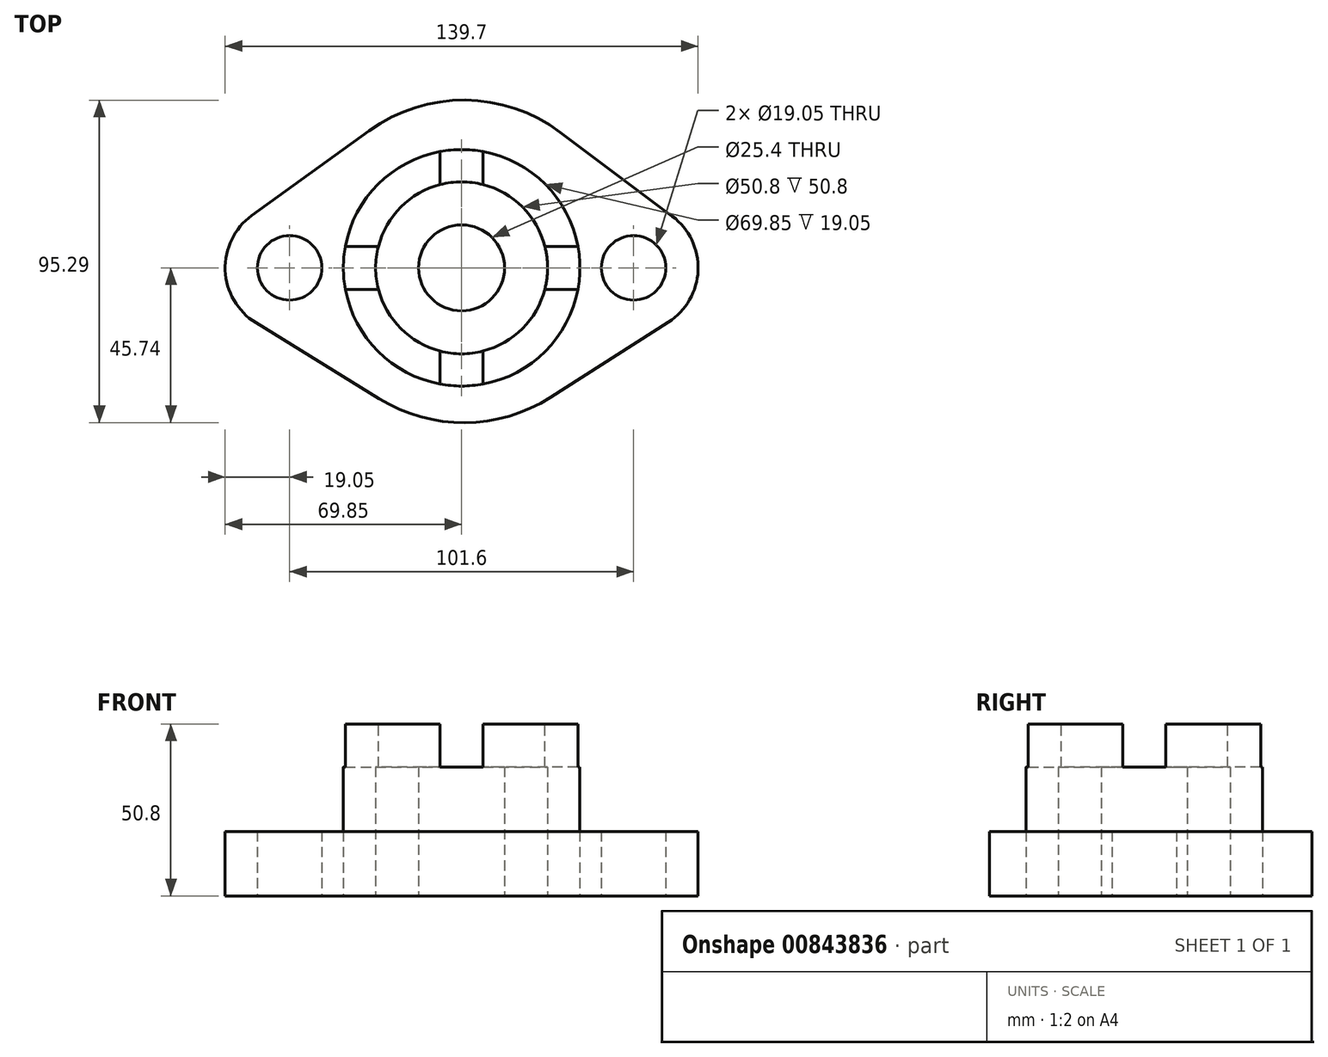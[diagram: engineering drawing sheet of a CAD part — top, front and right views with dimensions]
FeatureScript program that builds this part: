
annotation { "Feature Type Name" : "Feature", "Feature Type Description" : "" }
export const myFeature = defineFeature(function(context is Context, id is Id, definition is map)
    precondition{}
    {
        {
            var Q0;
            Q0=qCreatedBy(makeId("Top.planeOp"),FACE);
            var sketch = newSketch(context, id + "F0", { "sketchPlane" : qUnion([Q0])});
            skCircle(sketch, "E0", {"center": v(0, 0) * mm, "radius": 12.7 * mm});
            skCircle(sketch, "E1", {"center": v(0, 0) * mm, "radius": 34.93 * mm});
            skCircle(sketch, "E2", {"center": v(0, 0) * mm, "radius": 25.4 * mm});
            skLineSegment(sketch, "E3", {"start": v(0, 0) * mm, "end": v(88.9, 0) * mm, "construction": true});
            skLineSegment(sketch, "E4", {"start": v(88.9, 0) * mm, "end": v(-88.9, 0) * mm, "construction": true});
            skCircle(sketch, "E5", {"center": v(-50.8, 0) * mm, "radius": 9.53 * mm});
            skCircle(sketch, "E6", {"center": v(50.8, 0) * mm, "radius": 9.53 * mm});
            skArc(sketch, "E7", {"start": v(-61.97, 15.43) * mm, "mid": v(-69.84, -0.7) * mm, "end": v(-60.8, -16.22) * mm});
            skArc(sketch, "E8", {"start": v(61.05, -16.06) * mm, "mid": v(69.84, -0.72) * mm, "end": v(62.23, 15.24) * mm});
            skArc(sketch, "E9.trimOffspring", {"start": v(-24.37, -38.66) * mm, "mid": v(1, -45.74) * mm, "end": v(26.25, -38.26) * mm});
            skArc(sketch, "E10.trimOffspring", {"start": v(29.22, 40.01) * mm, "mid": v(1.04, 49.55) * mm, "end": v(-27.3, 40.5) * mm});
            skLineSegment(sketch, "E11", {"start": v(-61.97, 15.43) * mm, "end": v(-27.3, 40.5) * mm});
            skLineSegment(sketch, "E12", {"start": v(-60.8, -16.22) * mm, "end": v(-24.37, -38.66) * mm});
            skLineSegment(sketch, "E13", {"start": v(62.23, 15.24) * mm, "end": v(29.22, 40.01) * mm});
            skLineSegment(sketch, "E14", {"start": v(61.05, -16.06) * mm, "end": v(26.25, -38.26) * mm});
            skPoint(sketch, "E14.endSnap0", {"position": v(14.53, -43.66) * mm});
            skPoint(sketch, "E15.orphan", {"position": v(14.53, -45.74) * mm});
            skLineSegment(sketch, "E16", {"start": v(0, 0) * mm, "end": v(0, -51.53) * mm, "construction": true});
            skLineSegment(sketch, "E17", {"start": v(0, -51.53) * mm, "end": v(0, 57.86) * mm, "construction": true});
            skLineSegment(sketch, "E18", {"start": v(-30.1, 6.35) * mm, "end": v(-34.34, 6.35) * mm});
            skLineSegment(sketch, "E19", {"start": v(-30.1, 6.35) * mm, "end": v(-24.6, 6.35) * mm});
            skLineSegment(sketch, "E20", {"start": v(-30.1, -6.35) * mm, "end": v(-34.34, -6.35) * mm});
            skLineSegment(sketch, "E21", {"start": v(-30.1, -6.35) * mm, "end": v(-24.6, -6.35) * mm});
            skLineSegment(sketch, "E22", {"start": v(30.44, 6.35) * mm, "end": v(34.34, 6.35) * mm});
            skLineSegment(sketch, "E23", {"start": v(30.44, 6.35) * mm, "end": v(24.6, 6.35) * mm});
            skLineSegment(sketch, "E24", {"start": v(30.44, -6.35) * mm, "end": v(34.34, -6.35) * mm});
            skLineSegment(sketch, "E25", {"start": v(30.44, -6.35) * mm, "end": v(24.6, -6.35) * mm});
            skLineSegment(sketch, "E26", {"start": v(-6.35, 30.62) * mm, "end": v(-6.35, 34.34) * mm});
            skLineSegment(sketch, "E27", {"start": v(-6.35, 34.34) * mm, "end": v(-6.35, 24.6) * mm});
            skLineSegment(sketch, "E28", {"start": v(6.35, 30.62) * mm, "end": v(6.35, 34.34) * mm});
            skLineSegment(sketch, "E29", {"start": v(6.35, 34.34) * mm, "end": v(6.35, 24.6) * mm});
            skPoint(sketch, "E29.endSnap0", {"position": v(6.35, 32.48) * mm});
            skLineSegment(sketch, "E30", {"start": v(-6.35, -30.57) * mm, "end": v(-6.35, -24.6) * mm});
            skLineSegment(sketch, "E31", {"start": v(-6.35, -24.6) * mm, "end": v(-6.35, -34.34) * mm});
            skLineSegment(sketch, "E32", {"start": v(6.35, -30.57) * mm, "end": v(6.35, -24.6) * mm});
            skLineSegment(sketch, "E33", {"start": v(6.35, -24.6) * mm, "end": v(6.35, -34.34) * mm});
            skSolve(sketch);
        }
        {
            var Q0;
            Q0=makeQuery(id+"F0.imprint","IMPRINT",FACE,{"disambiguationData":[TD([[makeQuery(id+"F0.imprint","IMPRINT",EDGE,{"derivedFrom":sQuery(id+"F0.wireOp",EDGE,"E1")}),-1.0]])]});
            extrude(context, id + "F1", {"entities" : qUnion([Q0]), "depth" : 19.05 * mm, "offsetDistance" : 25.4 * mm});
        }
        {
            var Q0;
            Q0=makeQuery(id+"F0.imprint","IMPRINT",FACE,{"disambiguationData":[TD([[makeQuery(id+"F0.imprint","IMPRINT",EDGE,{"derivedFrom":sQuery(id+"F0.wireOp",EDGE,"E0")}),-1.0]])]});
            extrude(context, id + "F2", {"entities" : qUnion([Q0]), "depth" : 38.1 * mm, "offsetDistance" : 25.4 * mm});
        }
        {
            var Q0;
            Q0=makeQuery(id+"F0.imprint","IMPRINT",FACE,{"disambiguationData":[TD([[makeQuery(id+"F0.imprint","IMPRINT",EDGE,{"derivedFrom":sQuery(id+"F0.wireOp",EDGE,"E1")}),1.0]])]});
            extrude(context, id + "F3", {"entities" : qUnion([Q0]), "depth" : 50.8 * mm, "offsetDistance" : 25.4 * mm});
        }
        {
            var Q0;
            Q0=makeQuery(id+"F3.opExtrude","CAP_FACE",FACE,{"disambiguationData":[OSD([sQuery(id+"F0.wireOp",EDGE,"E1"),sQuery(id+"F0.wireOp",EDGE,"E2")])],"isStart":false});
            var sketch = newSketch(context, id + "F4", { "sketchPlane" : qUnion([Q0])});
            skLineSegment(sketch, "E34.left", {"start": v(6.35, 34.34) * mm, "end": v(6.35, 24.6) * mm});
            skLineSegment(sketch, "E34.right", {"start": v(-6.35, 34.34) * mm, "end": v(-6.35, 24.6) * mm});
            skPoint(sketch, "E34.middle", {"position": v(0, 25.4) * mm});
            skLineSegment(sketch, "E35.bottom", {"start": v(34.34, -6.35) * mm, "end": v(24.6, -6.35) * mm});
            skLineSegment(sketch, "E35.top", {"start": v(34.34, 6.35) * mm, "end": v(24.6, 6.35) * mm});
            skPoint(sketch, "E35.middle", {"position": v(25.4, 0) * mm});
            skLineSegment(sketch, "E36.left", {"start": v(6.35, -34.34) * mm, "end": v(6.35, -24.6) * mm});
            skLineSegment(sketch, "E36.right", {"start": v(-6.35, -34.34) * mm, "end": v(-6.35, -24.6) * mm});
            skPoint(sketch, "E36.middle", {"position": v(0, -25.4) * mm});
            skLineSegment(sketch, "E37.bottom", {"start": v(-34.34, 6.35) * mm, "end": v(-24.6, 6.35) * mm});
            skLineSegment(sketch, "E37.top", {"start": v(-34.34, -6.35) * mm, "end": v(-24.6, -6.35) * mm});
            skPoint(sketch, "E37.middle", {"position": v(-25.4, 0) * mm});
            skPoint(sketch, "E38", {"position": v(-24.6, 6.35) * mm});
            skPoint(sketch, "E39", {"position": v(-24.6, -6.35) * mm});
            skPoint(sketch, "E40", {"position": v(6.35, -24.6) * mm});
            skPoint(sketch, "E40.positionSnap0", {"position": v(6.35, -25.4) * mm});
            skPoint(sketch, "E41", {"position": v(-6.35, -24.6) * mm});
            skPoint(sketch, "E42", {"position": v(24.6, 6.35) * mm});
            skPoint(sketch, "E43", {"position": v(24.6, -6.35) * mm});
            skPoint(sketch, "E44", {"position": v(6.35, 24.6) * mm});
            skPoint(sketch, "E45", {"position": v(-6.35, 24.6) * mm});
            skPoint(sketch, "E46.orphan", {"position": v(-16.46, 6.35) * mm});
            skPoint(sketch, "E47.orphan", {"position": v(-16.46, -6.35) * mm});
            skPoint(sketch, "E36.top.start.orphan", {"position": v(6.35, -16.46) * mm});
            skPoint(sketch, "E48.orphan", {"position": v(-6.35, -16.46) * mm});
            skPoint(sketch, "E35.right.end.orphan", {"position": v(16.46, 6.35) * mm});
            skPoint(sketch, "E49.orphan", {"position": v(16.46, -6.35) * mm});
            skPoint(sketch, "E34.top.start.orphan", {"position": v(6.35, 16.46) * mm});
            skPoint(sketch, "E50.orphan", {"position": v(-6.35, 16.46) * mm});
            skSolve(sketch);
        }
        {
            var Q0;
            {var subQ0=sQuery(id+"F4.wireOp",EDGE,"E36.left");Q0=makeQuery(id+"F4.imprint","IMPRINT",FACE,{"disambiguationData":[TD([[makeQuery(id+"F4.imprint","IMPRINT",EDGE,{"derivedFrom":subQ0}),1.0]])]});}
            var Q1;
            {var subQ0=sQuery(id+"F4.wireOp",EDGE,"E37.bottom");Q1=makeQuery(id+"F4.imprint","IMPRINT",FACE,{"disambiguationData":[TD([[makeQuery(id+"F4.imprint","IMPRINT",EDGE,{"derivedFrom":subQ0}),-1.0]])]});}
            var Q2;
            {var subQ0=sQuery(id+"F4.wireOp",EDGE,"E34.left");Q2=makeQuery(id+"F4.imprint","IMPRINT",FACE,{"disambiguationData":[TD([[makeQuery(id+"F4.imprint","IMPRINT",EDGE,{"derivedFrom":subQ0}),-1.0]])]});}
            var Q3;
            {var subQ0=sQuery(id+"F4.wireOp",EDGE,"E35.bottom");Q3=makeQuery(id+"F4.imprint","IMPRINT",FACE,{"disambiguationData":[TD([[makeQuery(id+"F4.imprint","IMPRINT",EDGE,{"derivedFrom":subQ0}),-1.0]])]});}
            extrude(context, id + "F5", {"entities" : qUnion([Q0, Q1, Q2, Q3]), "operationType" : NewBodyOperationType.REMOVE, "oppositeDirection" : true, "depth" : 12.7 * mm, "offsetDistance" : 25.4 * mm});
        }
    });
